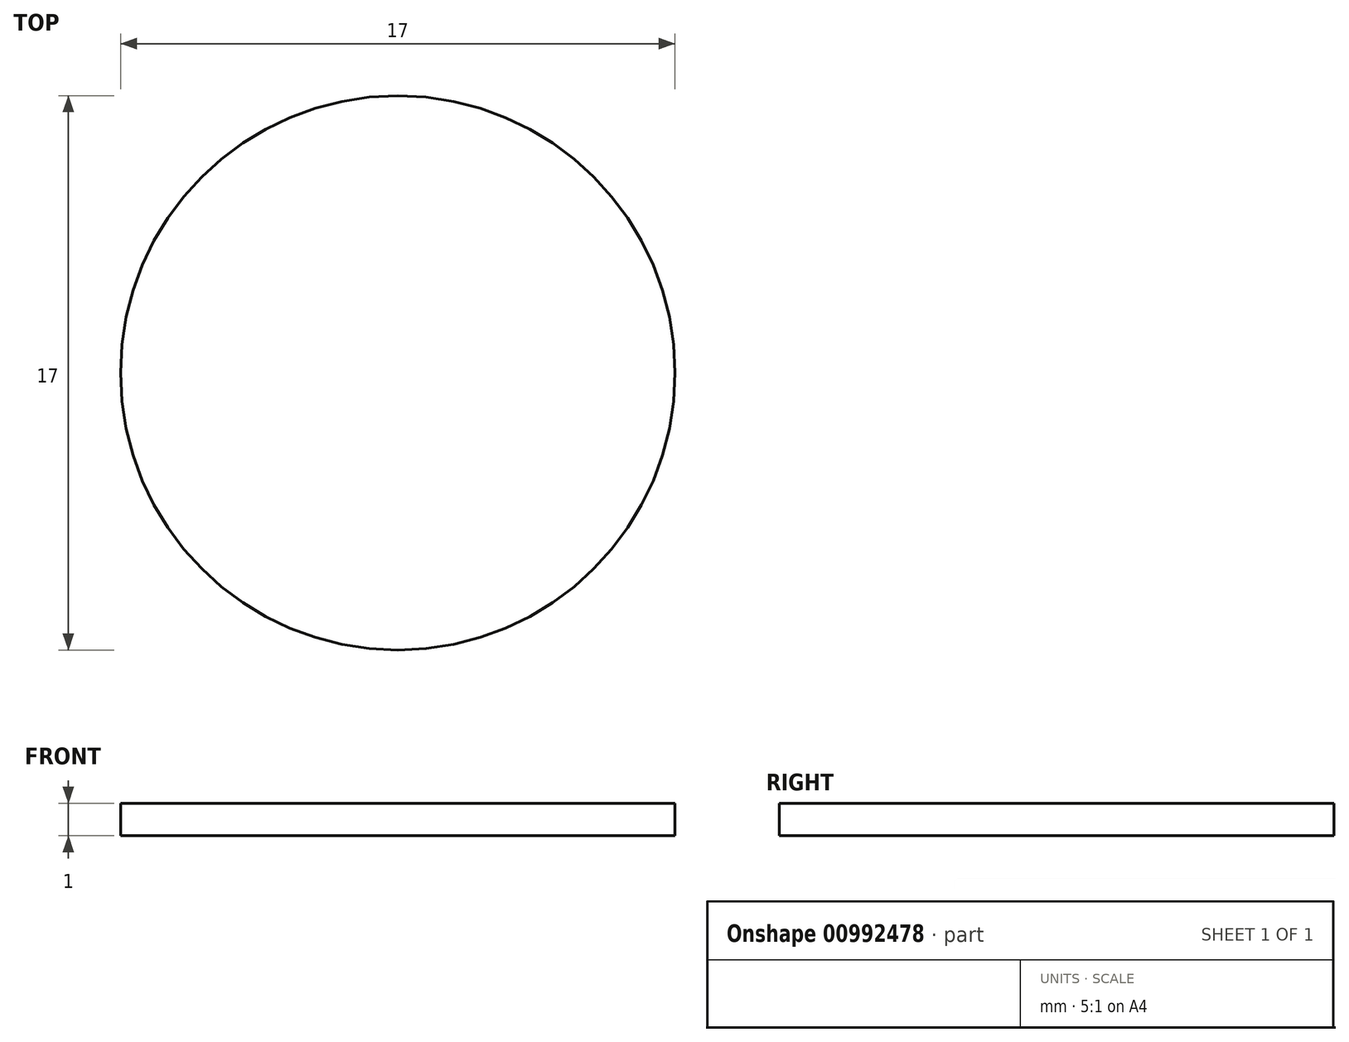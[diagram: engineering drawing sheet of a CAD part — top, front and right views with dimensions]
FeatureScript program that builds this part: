
annotation { "Feature Type Name" : "Feature", "Feature Type Description" : "" }
export const myFeature = defineFeature(function(context is Context, id is Id, definition is map)
    precondition{}
    {
        {
            var Q0;
            Q0=qCreatedBy(makeId("Top.planeOp"),FACE);
            var sketch = newSketch(context, id + "F0", { "sketchPlane" : qUnion([Q0])});
            skCircle(sketch, "E0", {"center": v(0, 0) * mm, "radius": 8.5 * mm});
            skSolve(sketch);
        }
        {
            var Q0;
            Q0 = qSketchRegion(id + "F0", true);
            extrude(context, id + "F1", {"entities" : qUnion([Q0]), "depth" : 1 * mm, "offsetDistance" : 25 * mm});
        }
    });
